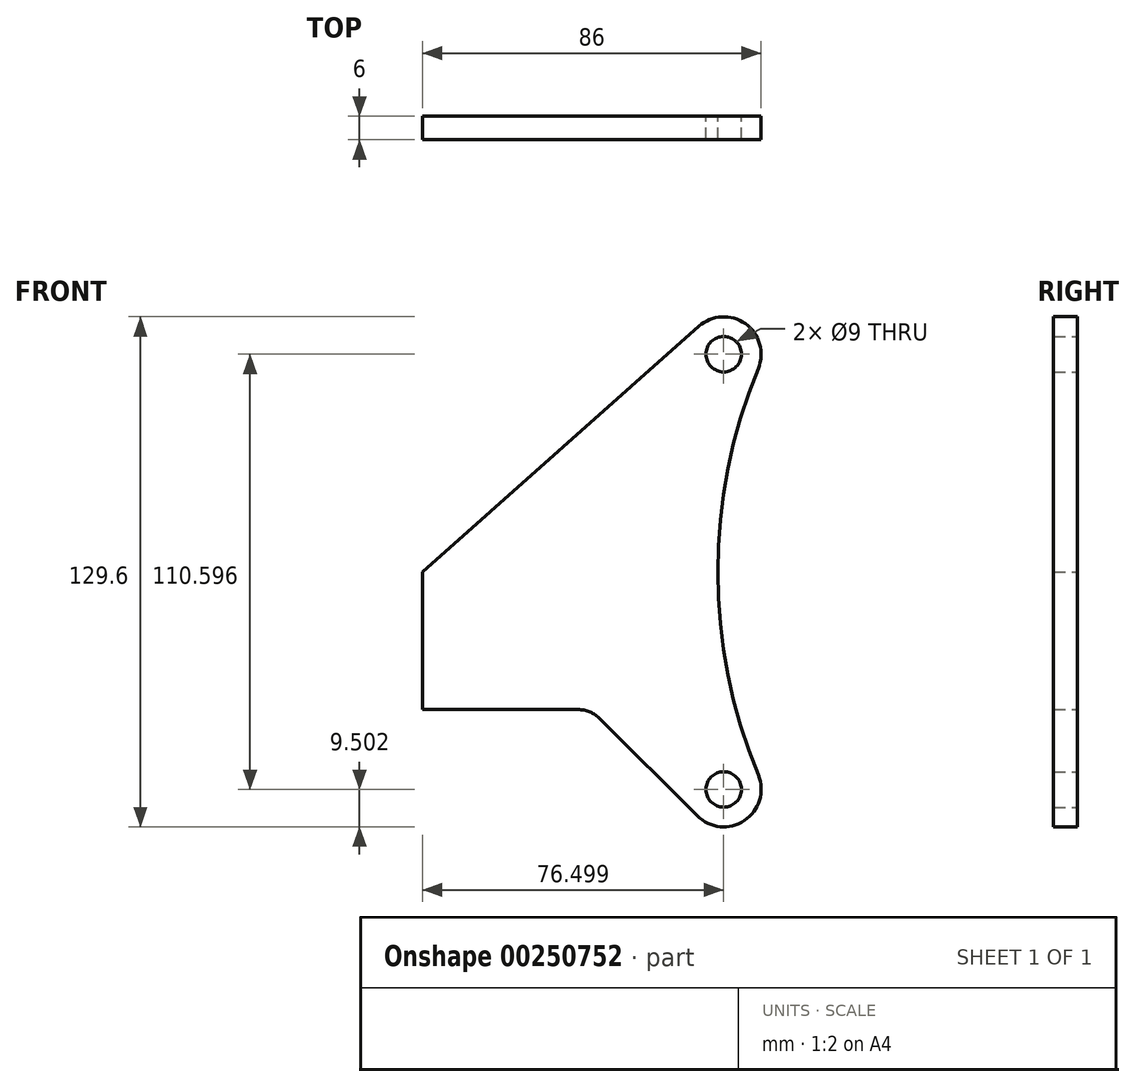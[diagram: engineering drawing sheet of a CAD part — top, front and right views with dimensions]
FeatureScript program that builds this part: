
annotation { "Feature Type Name" : "Feature", "Feature Type Description" : "" }
export const myFeature = defineFeature(function(context is Context, id is Id, definition is map)
    precondition{}
    {
        {
            var Q0;
            Q0=qCreatedBy(makeId("Front.planeOp"),FACE);
            var sketch = newSketch(context, id + "F0", { "sketchPlane" : qUnion([Q0])});
            skCircle(sketch, "E0", {"center": v(0, 0) * mm, "radius": 144.5 * mm, "construction": true});
            skCircle(sketch, "E1", {"center": v(55.3, 133.5) * mm, "radius": 4.5 * mm, "construction": true});
            skCircle(sketch, "E2.1.0", {"center": v(-55.3, 133.5) * mm, "radius": 4.5 * mm, "construction": true});
            skCircle(sketch, "E2.2.0", {"center": v(-133.5, 55.3) * mm, "radius": 4.5 * mm});
            skCircle(sketch, "E2.3.0", {"center": v(-133.5, -55.3) * mm, "radius": 4.5 * mm});
            skCircle(sketch, "E2.4.0", {"center": v(-55.3, -133.5) * mm, "radius": 4.5 * mm, "construction": true});
            skCircle(sketch, "E2.5.0", {"center": v(55.3, -133.5) * mm, "radius": 4.5 * mm, "construction": true});
            skCircle(sketch, "E2.6.0", {"center": v(133.5, -55.3) * mm, "radius": 4.5 * mm, "construction": true});
            skCircle(sketch, "E2.7.0", {"center": v(133.5, 55.3) * mm, "radius": 4.5 * mm, "construction": true});
            skLineSegment(sketch, "E3", {"start": v(0, 0) * mm, "end": v(0, 172.97) * mm, "construction": true});
            skLineSegment(sketch, "E4", {"start": v(0, 0) * mm, "end": v(55.3, 133.5) * mm, "construction": true});
            skArc(sketch, "E5.0", {"start": v(-124.72, -51.66) * mm, "mid": v(-135, 0) * mm, "end": v(-124.72, 51.66) * mm});
            skLineSegment(sketch, "E6", {"start": v(-210, -35) * mm, "end": v(-170.55, -35) * mm});
            skArc(sketch, "E7.0", {"start": v(-140.22, -62.02) * mm, "mid": v(-128.22, -63.2) * mm, "end": v(-124.72, -51.66) * mm});
            skArc(sketch, "E8.0", {"start": v(-124.72, 51.66) * mm, "mid": v(-128, 63.04) * mm, "end": v(-139.81, 62.4) * mm});
            skLineSegment(sketch, "E9", {"start": v(-140.22, -62.02) * mm, "end": v(-164.9, -37.34) * mm});
            skPoint(sketch, "E10.visualSharp", {"position": v(-167.23, -35) * mm});
            skLineSegment(sketch, "E11", {"start": v(-185, -73.36) * mm, "end": v(-185, 53.36) * mm, "construction": true});
            skLineSegment(sketch, "E12", {"start": v(-210, -20) * mm, "end": v(-150, -20) * mm, "construction": true});
            skLineSegment(sketch, "E13", {"start": v(-150, -20) * mm, "end": v(-150, 40) * mm, "construction": true});
            skLineSegment(sketch, "E14", {"start": v(-150, 40) * mm, "end": v(-156, 40) * mm, "construction": true});
            skLineSegment(sketch, "E15", {"start": v(-156, 40) * mm, "end": v(-156, -14) * mm, "construction": true});
            skLineSegment(sketch, "E16", {"start": v(-156, -14) * mm, "end": v(-210, -14) * mm, "construction": true});
            skLineSegment(sketch, "E17", {"start": v(-210, -14) * mm, "end": v(-210, -20) * mm, "construction": true});
            skLineSegment(sketch, "E18", {"start": v(-210, -35) * mm, "end": v(-210, 0) * mm});
            skLineSegment(sketch, "E19", {"start": v(-210, 0) * mm, "end": v(-139.81, 62.4) * mm});
            skPoint(sketch, "E20.visualSharp", {"position": v(-210, 0) * mm});
            skArc(sketch, "E21.filletArc", {"start": v(-164.9, -37.34) * mm, "mid": v(-167.49, -35.6) * mm, "end": v(-170.55, -35) * mm});
            skSolve(sketch);
        }
        {
            var Q0;
            Q0=qSketchRegion(id+"F0",true);
            extrude(context, id + "F1", {"entities" : qUnion([Q0]), "depth" : 6 * mm});
        }
    });
